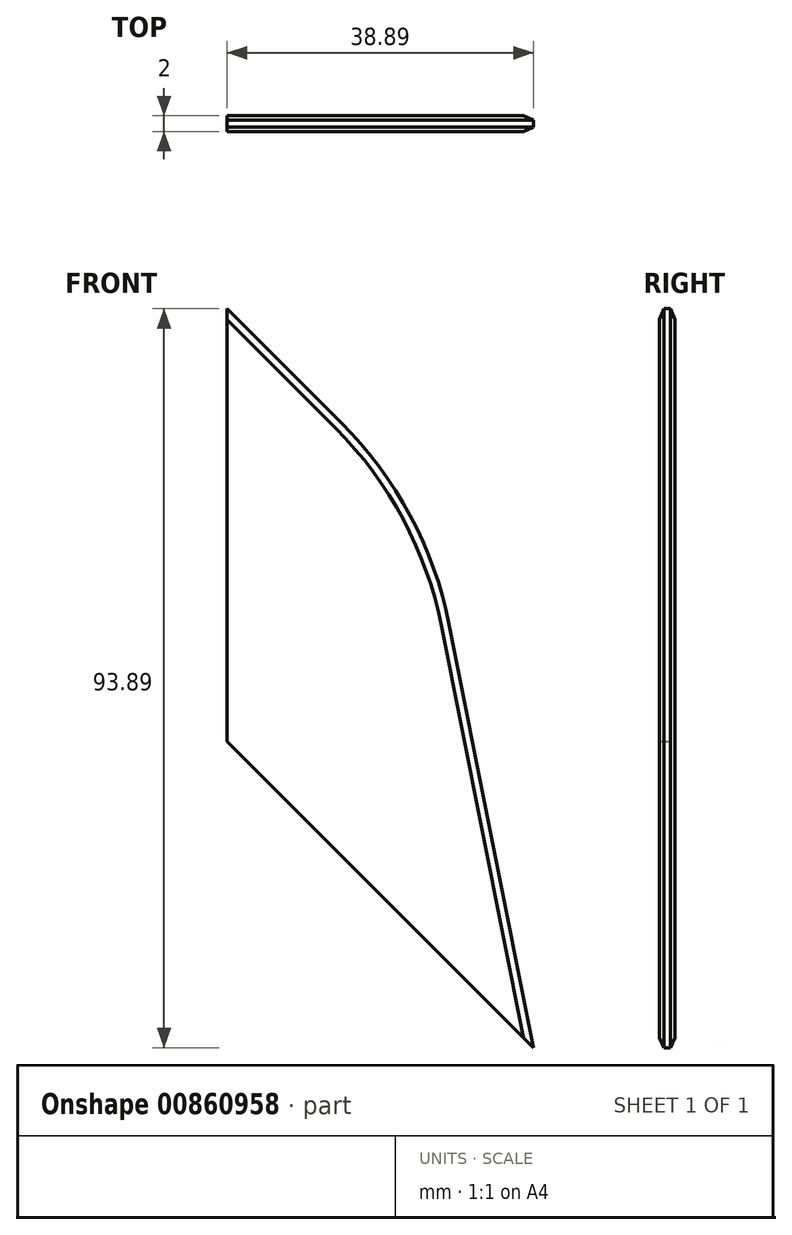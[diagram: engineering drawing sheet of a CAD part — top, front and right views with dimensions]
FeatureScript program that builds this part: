
annotation { "Feature Type Name" : "Feature", "Feature Type Description" : "" }
export const myFeature = defineFeature(function(context is Context, id is Id, definition is map)
    precondition{}
    {
        {
            var Q0;
            Q0=qCreatedBy(makeId("Front.planeOp"),FACE);
            var sketch = newSketch(context, id + "F0", { "sketchPlane" : qUnion([Q0])});
            skLineSegment(sketch, "E0", {"start": v(0, 0) * mm, "end": v(0, 55) * mm});
            skLineSegment(sketch, "E1", {"start": v(0, 0) * mm, "end": v(38.9, -38.9) * mm});
            skLineSegment(sketch, "E2", {"start": v(38.9, -38.9) * mm, "end": v(25.24, 29.76) * mm});
            skLineSegment(sketch, "E3", {"start": v(0, 55) * mm, "end": v(25.24, 29.76) * mm});
            skSolve(sketch);
        }
        {
            var Q0;
            Q0 = qSketchRegion(id + "F0", true);
            extrude(context, id + "F1", {"entities" : qUnion([Q0]), "depth" : 2 * mm, "offsetDistance" : 25 * mm});
        }
        {
            var Q0;
            Q0=makeQuery(id+"F1.opExtrude","SWEPT_EDGE",EDGE,{"disambiguationData":[OSD([sQuery(id+"F0.wireOp",EDGE,"E2"),sQuery(id+"F0.wireOp",EDGE,"E3")])]});
            fillet(context, id + "F2", {"entities" : qUnion([Q0]), "radius" : 50 * mm, "tangentPropagation" : true, "allowEdgeOverflow" : false});
        }
        {
            var Q0;
            Q0=makeQuery(id+"F1.opExtrude","CAP_EDGE",EDGE,{"disambiguationData":[OSD([sQuery(id+"F0.wireOp",EDGE,"E3")])],"isStart":false});
            var Q1;
            Q1=makeQuery(id+"F1.opExtrude","CAP_EDGE",EDGE,{"disambiguationData":[OSD([sQuery(id+"F0.wireOp",EDGE,"E3")])],"isStart":true});
            chamfer(context, id + "F3", {"entities" : qUnion([Q0, Q1]), "chamferType" : ChamferType.OFFSET_ANGLE, "width" : 1 * mm, "oppositeDirection" : false, "angle" : 30 * degree, "tangentPropagation" : true});
        }
    });
